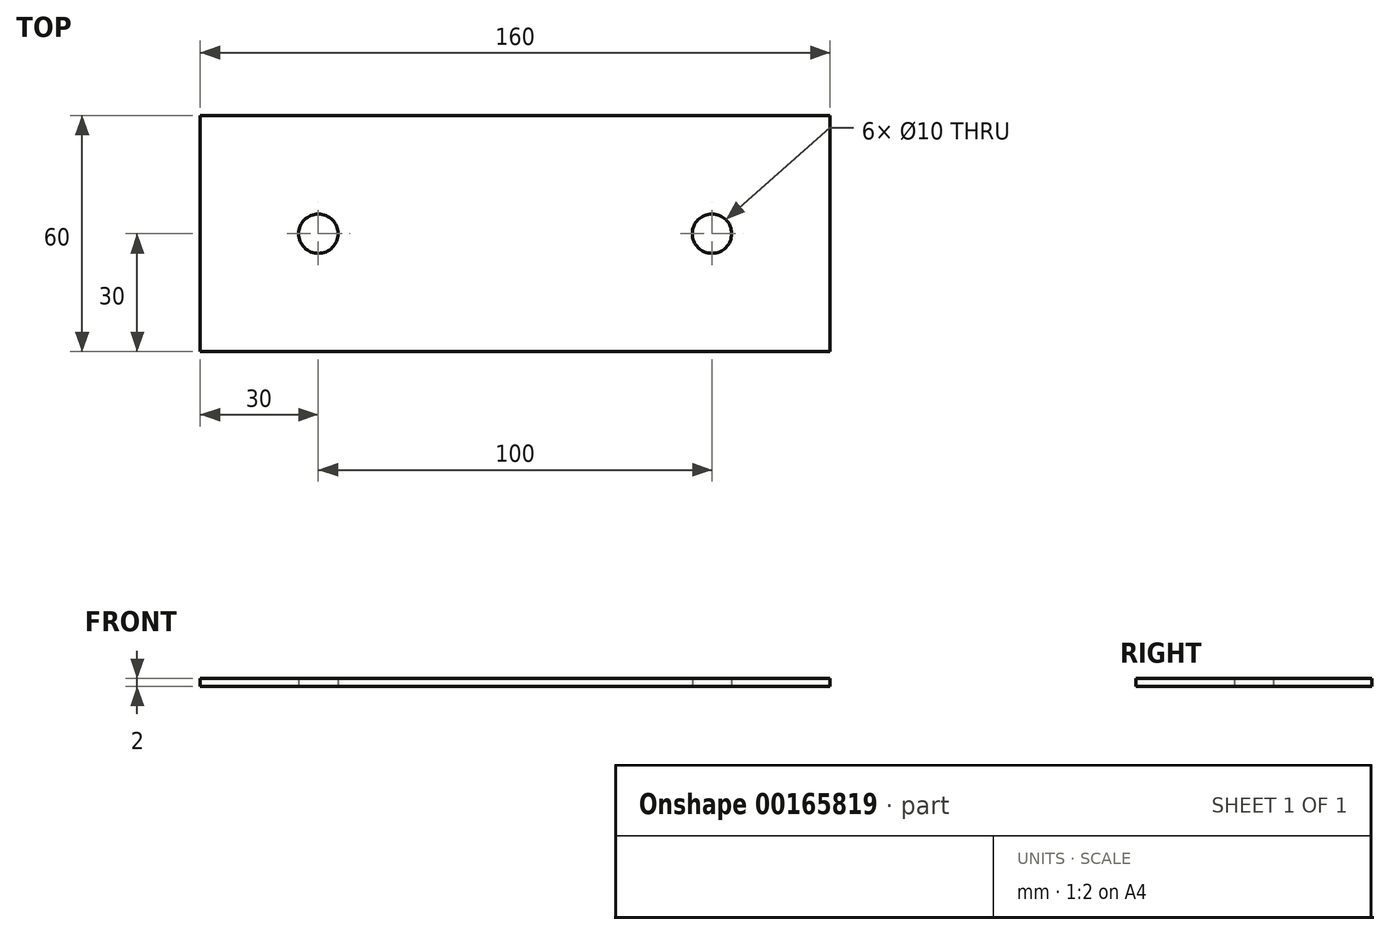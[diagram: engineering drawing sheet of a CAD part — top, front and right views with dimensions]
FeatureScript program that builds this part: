
annotation { "Feature Type Name" : "Feature", "Feature Type Description" : "" }
export const myFeature = defineFeature(function(context is Context, id is Id, definition is map)
    precondition{}
    {
        {
            var Q0;
            Q0=qCreatedBy(makeId("Top.planeOp"),FACE);
            var sketch = newSketch(context, id + "F0", { "sketchPlane" : qUnion([Q0])});
            skLineSegment(sketch, "E0.bottom", {"start": v(-80, -30) * mm, "end": v(80, -30) * mm});
            skLineSegment(sketch, "E0.top", {"start": v(-80, 30) * mm, "end": v(80, 30) * mm});
            skLineSegment(sketch, "E0.left", {"start": v(-80, -30) * mm, "end": v(-80, 30) * mm});
            skLineSegment(sketch, "E0.right", {"start": v(80, -30) * mm, "end": v(80, 30) * mm});
            skCircle(sketch, "E1", {"center": v(-50, 0) * mm, "radius": 5 * mm});
            skCircle(sketch, "E2", {"center": v(50, 0) * mm, "radius": 5 * mm});
            skLineSegment(sketch, "E3", {"start": v(-80, 30) * mm, "end": v(-50, 0) * mm, "construction": true});
            skLineSegment(sketch, "E4", {"start": v(50, 0) * mm, "end": v(80, -30) * mm, "construction": true});
            skLineSegment(sketch, "E5", {"start": v(-80, -30) * mm, "end": v(-50, 0) * mm, "construction": true});
            skLineSegment(sketch, "E6", {"start": v(80, 30) * mm, "end": v(50, 0) * mm, "construction": true});
            skLineSegment(sketch, "E7", {"start": v(-50, 0) * mm, "end": v(50, 0) * mm, "construction": true});
            skSolve(sketch);
        }
        {
            var Q0;
            Q0=makeQuery(id+"F0.imprint","IMPRINT",FACE,{"disambiguationData":[TD([[makeQuery(id+"F0.imprint","IMPRINT",EDGE,{"derivedFrom":sQuery(id+"F0.wireOp",EDGE,"E0.bottom")}),1.0]])]});
            extrude(context, id + "F1", {"entities" : qUnion([Q0]), "depth" : 2 * mm});
        }
    });
